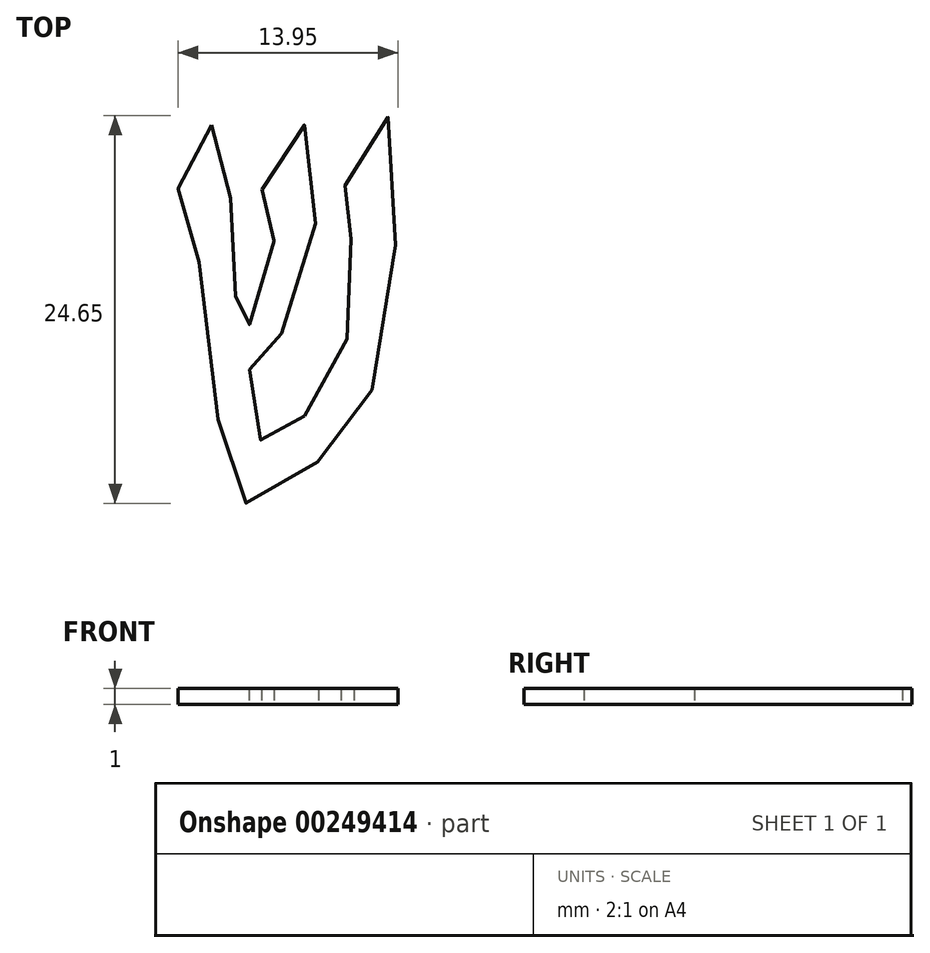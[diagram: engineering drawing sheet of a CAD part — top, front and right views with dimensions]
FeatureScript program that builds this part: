
annotation { "Feature Type Name" : "Feature", "Feature Type Description" : "" }
export const myFeature = defineFeature(function(context is Context, id is Id, definition is map)
    precondition{}
    {
        {
            var Q0;
            Q0=qCreatedBy(makeId("Top.planeOp"),FACE);
            var sketch = newSketch(context, id + "F0", { "sketchPlane" : qUnion([Q0])});
            skLineSegment(sketch, "E0.bottom", {"start": v(13, 58.83) * mm, "end": v(-13, 58.83) * mm});
            skLineSegment(sketch, "E0.top", {"start": v(13, -61.17) * mm, "end": v(-13, -61.17) * mm});
            skLineSegment(sketch, "E0.left", {"start": v(13, 58.83) * mm, "end": v(13, -61.17) * mm});
            skLineSegment(sketch, "E0.right", {"start": v(-13, 58.83) * mm, "end": v(-13, -61.17) * mm});
            skPoint(sketch, "E0.middle", {"position": v(0, -1.17) * mm});
            skSolve(sketch);
        }
        {
            var Q0;
            Q0=makeQuery(id+"F0.imprint","IMPRINT",FACE,{"disambiguationData":[TD([[makeQuery(id+"F0.imprint","IMPRINT",EDGE,{"derivedFrom":sQuery(id+"F0.wireOp",EDGE,"E0.bottom")}),1.0]])]});
            var sketch = newSketch(context, id + "F1", { "sketchPlane" : qUnion([Q0])});
            skFitSpline(sketch, "E1", {"points": [v(-4.81, 52.83) * mm, v(-6.93, 49.02) * mm, v(-6.39, 47.68) * mm, v(-4.15, 32.36) * mm, v(-2.33, 28.79) * mm, v(2.88, 32.36) * mm, v(6.15, 39.08) * mm, v(6.15, 53.44) * mm, v(3.42, 48.05) * mm, v(3.73, 46.9) * mm, v(4.03, 40.42) * mm, v(1.3, 34.6) * mm, v(-1.24, 32.6) * mm, v(-1.9, 33.27) * mm, v(-2.33, 37.63) * mm, v(-1.48, 38.48) * mm, v(1.12, 42.96) * mm, v(1.12, 52.83) * mm, v(-1.6, 48.9) * mm, v(-1.3, 47.62) * mm, v(-1.06, 43.32) * mm, v(-3, 39.63) * mm, v(-3.3, 41.39) * mm, v(-3.66, 48.84) * mm, v(-4.81, 52.83) * mm]});
            skSolve(sketch);
        }
        {
            var Q0;
            Q0 = qSketchRegion(id + "F1", true);
            extrude(context, id + "F2", {"entities" : qUnion([Q0]), "depth" : 1 * mm});
        }
    });
